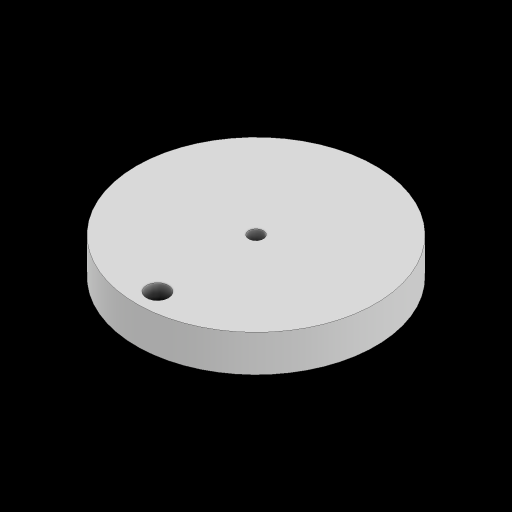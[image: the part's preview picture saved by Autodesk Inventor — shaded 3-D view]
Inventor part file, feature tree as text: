
AUTODESK INVENTOR PART (.ipt)
format: ipt  version: 2023 (Build 270158000, 158)  size: 138,752 bytes
history: native  units: mm
features: extrude x1, sketch x1
ambient origin geometry x8: Origin, YZ Plane, XZ Plane, XY Plane, X Axis, Y Axis, Z Axis, Center Point
bodies: Solid1 (feature_tree)
feature tree (2):
  extrude  "Extrusion1"  Depth=10.0mm
  sketch  "Sketch1"  dims[d1=120.0mm d2=200.0mm d3=15.0deg d4=10.0mm d5=10.0mm d6=79.8mm d7=360.0deg d8=10.0mm d9=4.0mm d10=10.0mm d11=65.0mm d12=6.0mm d13=10.0mm d14=0.0mm]
